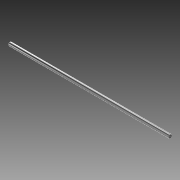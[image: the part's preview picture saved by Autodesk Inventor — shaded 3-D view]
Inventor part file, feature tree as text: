
AUTODESK INVENTOR PART (.ipt)
format: ipt  version: 2015 (Build 190159000, 159)  size: 79,360 bytes
history: native  units: mm
features: hole x2, revolve x1, chamfer x1
ambient origin geometry x8: Origin, YZ Plane, XZ Plane, XY Plane, X Axis, Y Axis, Z Axis, Center Point
bodies: Solid1 (feature_tree)
feature tree (4):
  revolve  "Revolución1"  [1 undecoded]
  hole  "Agujero1"  [1 undecoded]
  hole  "Agujero2"  [1 undecoded]
  chamfer  "Chaflán1"  Distance=0.5mm Angle=45.0deg
note: 3 required parameter values undecoded (feature->parameter linkage not recoverable at this tier; creation-order binding heuristic only, values carry confidence <= 0.55)